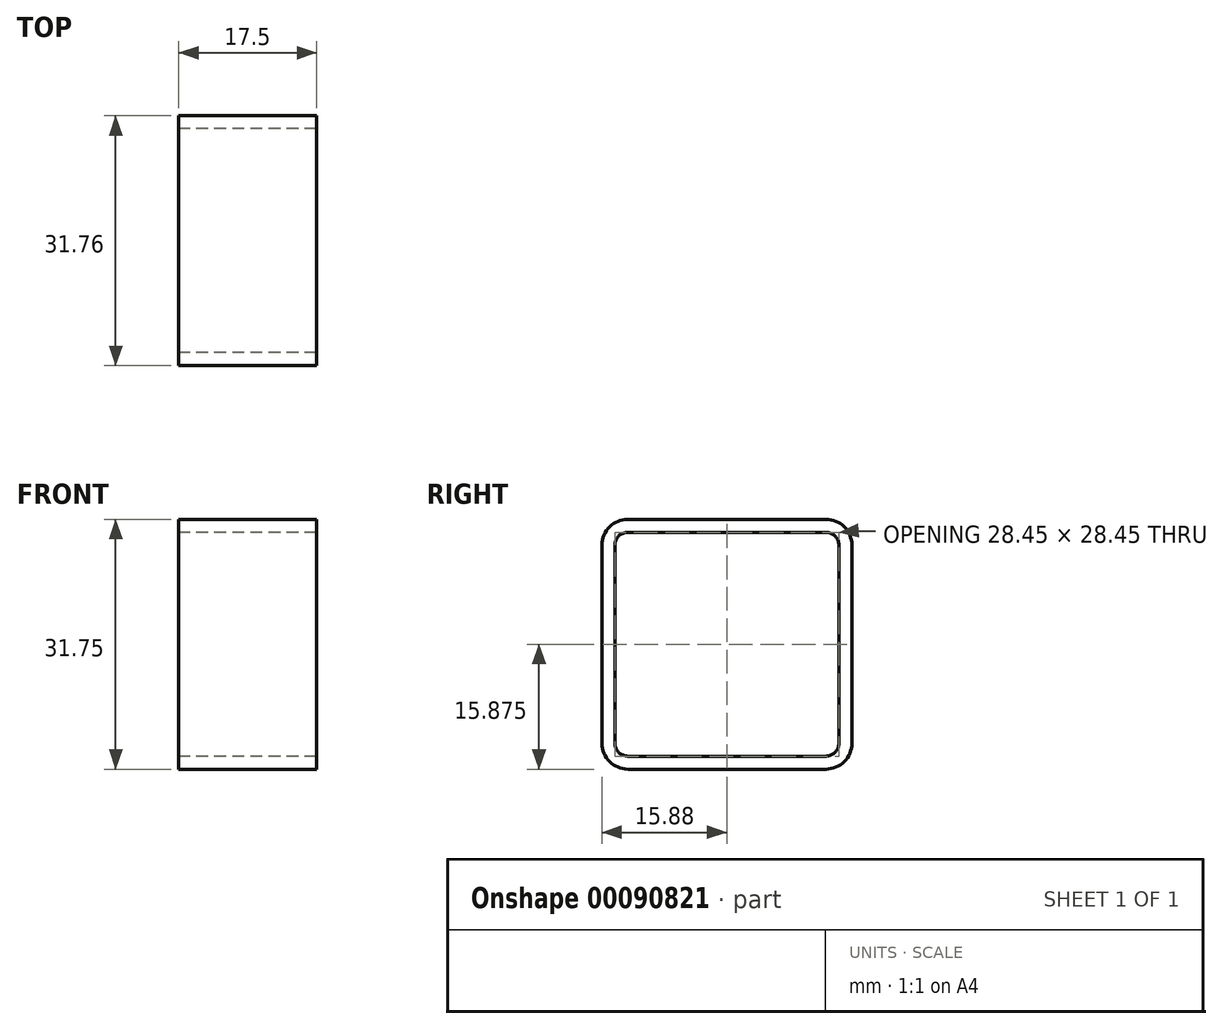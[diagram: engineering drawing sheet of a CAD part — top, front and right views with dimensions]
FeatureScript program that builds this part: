
annotation { "Feature Type Name" : "Feature", "Feature Type Description" : "" }
export const myFeature = defineFeature(function(context is Context, id is Id, definition is map)
    precondition{}
    {
        {
            var Q0;
            Q0=qCreatedBy(makeId("Top.planeOp"),FACE);
            var sketch = newSketch(context, id + "F0", { "sketchPlane" : qUnion([Q0])});
            skLineSegment(sketch, "E0.bottom", {"start": v(12.57, -15.88) * mm, "end": v(-12.57, -15.88) * mm});
            skLineSegment(sketch, "E0.top", {"start": v(12.57, 15.88) * mm, "end": v(-12.57, 15.88) * mm});
            skLineSegment(sketch, "E0.left", {"start": v(15.88, -12.57) * mm, "end": v(15.88, 12.57) * mm});
            skLineSegment(sketch, "E0.right", {"start": v(-15.88, -12.57) * mm, "end": v(-15.88, 12.57) * mm});
            skPoint(sketch, "E0.middle", {"position": v(0, 0) * mm});
            skPoint(sketch, "E1.visualSharp", {"position": v(-15.88, 15.87) * mm});
            skArc(sketch, "E1.filletArc", {"start": v(-12.57, 15.88) * mm, "mid": v(-14.9, 14.9) * mm, "end": v(-15.88, 12.57) * mm});
            skPoint(sketch, "E2.visualSharp", {"position": v(15.88, 15.88) * mm});
            skArc(sketch, "E2.filletArc", {"start": v(15.88, 12.57) * mm, "mid": v(14.9, 14.9) * mm, "end": v(12.57, 15.88) * mm});
            skPoint(sketch, "E3.visualSharp", {"position": v(15.87, -15.88) * mm});
            skArc(sketch, "E3.filletArc", {"start": v(12.57, -15.88) * mm, "mid": v(14.9, -14.9) * mm, "end": v(15.88, -12.57) * mm});
            skPoint(sketch, "E4.visualSharp", {"position": v(-15.88, -15.88) * mm});
            skArc(sketch, "E4.filletArc", {"start": v(-15.88, -12.57) * mm, "mid": v(-14.9, -14.9) * mm, "end": v(-12.57, -15.88) * mm});
            skLineSegment(sketch, "E5.0", {"start": v(12.57, 14.22) * mm, "end": v(-12.57, 14.22) * mm});
            skLineSegment(sketch, "E6.0", {"start": v(-14.22, -12.57) * mm, "end": v(-14.22, 12.57) * mm});
            skLineSegment(sketch, "E7.0", {"start": v(14.22, -12.57) * mm, "end": v(14.22, 12.57) * mm});
            skLineSegment(sketch, "E8.0", {"start": v(12.57, -14.22) * mm, "end": v(-12.57, -14.22) * mm});
            skArc(sketch, "E9.filletArc", {"start": v(-12.57, 14.22) * mm, "mid": v(-13.74, 13.74) * mm, "end": v(-14.22, 12.57) * mm});
            skArc(sketch, "E10.filletArc", {"start": v(14.22, 12.57) * mm, "mid": v(13.74, 13.74) * mm, "end": v(12.57, 14.22) * mm});
            skArc(sketch, "E11.filletArc", {"start": v(-14.22, -12.57) * mm, "mid": v(-13.74, -13.74) * mm, "end": v(-12.57, -14.22) * mm});
            skArc(sketch, "E12.filletArc", {"start": v(12.57, -14.22) * mm, "mid": v(13.74, -13.74) * mm, "end": v(14.22, -12.57) * mm});
            skSolve(sketch);
        }
        {
            assignVariable(context, id + "F1", {"name" : "L", "anyValue" : 17.5});
        }
        {
            var Q0;
            Q0=makeQuery(id+"F0.imprint","IMPRINT",FACE,{"disambiguationData":[TD([[makeQuery(id+"F0.imprint","IMPRINT",EDGE,{"derivedFrom":sQuery(id+"F0.wireOp",EDGE,"E0.bottom")}),-1.0]])]});
            extrude(context, id + "F2", {"entities" : qUnion([Q0]), "depth" : (getVariable(context, 'L')) * mm});
        }
        {
            var Q0;
            Q0=makeQuery(id+"F2.opExtrude","SWEPT_BODY",BODY,{"disambiguationData":[OSD([sQuery(id+"F0.wireOp",EDGE,"E0.bottom"),sQuery(id+"F0.wireOp",EDGE,"E0.top"),sQuery(id+"F0.wireOp",EDGE,"E0.left"),sQuery(id+"F0.wireOp",EDGE,"E0.right"),sQuery(id+"F0.wireOp",EDGE,"E1.filletArc"),sQuery(id+"F0.wireOp",EDGE,"E2.filletArc"),sQuery(id+"F0.wireOp",EDGE,"E3.filletArc"),sQuery(id+"F0.wireOp",EDGE,"E4.filletArc"),sQuery(id+"F0.wireOp",EDGE,"E5.0"),sQuery(id+"F0.wireOp",EDGE,"E6.0"),sQuery(id+"F0.wireOp",EDGE,"E7.0"),sQuery(id+"F0.wireOp",EDGE,"E8.0"),sQuery(id+"F0.wireOp",EDGE,"E9.filletArc"),sQuery(id+"F0.wireOp",EDGE,"E10.filletArc"),sQuery(id+"F0.wireOp",EDGE,"E11.filletArc"),sQuery(id+"F0.wireOp",EDGE,"E12.filletArc")])]});
            var Q1;
            Q1=makeQuery(id+"F2.opExtrude","CAP_EDGE",EDGE,{"disambiguationData":[OSD([sQuery(id+"F0.wireOp",EDGE,"E0.right")])],"isStart":false});
            var Q2;
            Q2=makeQuery(id+"F2.opExtrude","CAP_EDGE",EDGE,{"disambiguationData":[OSD([sQuery(id+"F0.wireOp",EDGE,"E0.right")])],"isStart":false});
            transform(context, id + "F3", {"entities" : qUnion([Q0]), "transformType" : TransformType.ROTATION, "transformAxis" : qUnion([Q2]), "angle" : 90 * degree, "makeCopy" : false});
        }
        {
            var Q0;
            Q0=makeQuery(id+"F2.opExtrude","SWEPT_FACE",FACE,{"disambiguationData":[OSD([sQuery(id+"F0.wireOp",EDGE,"E0.right")])]});
            var sketch = newSketch(context, id + "F4", { "sketchPlane" : qUnion([Q0])});
            skPoint(sketch, "E13", {"position": v(-412.75, -4.76) * mm});
            skPoint(sketch, "E14", {"position": v(-63.5, -4.76) * mm});
            skSolve(sketch);
        }
    });
